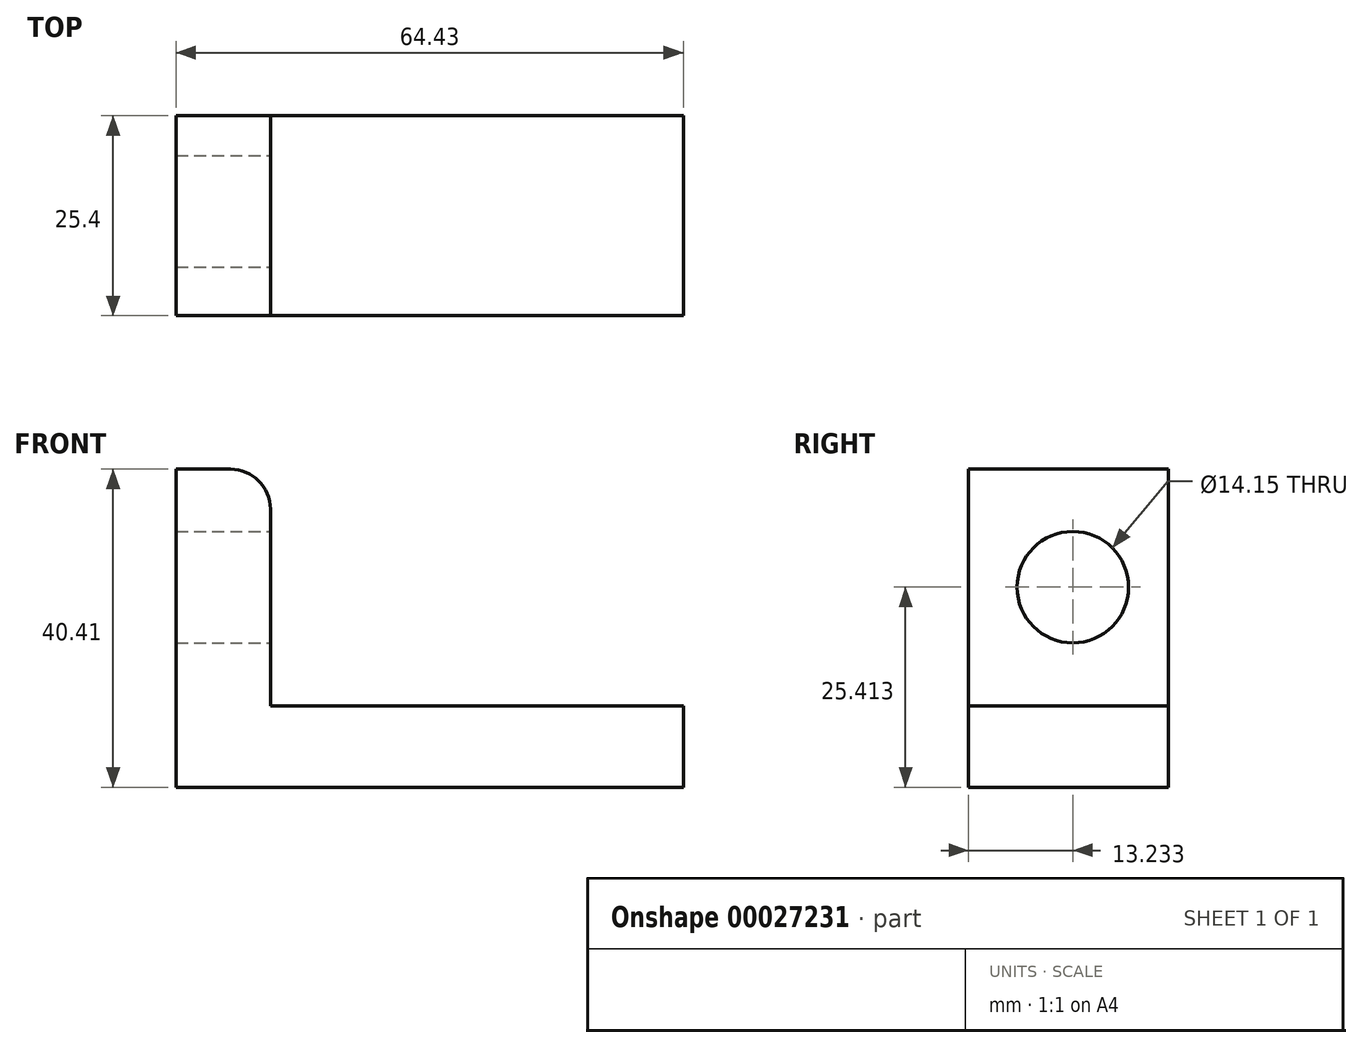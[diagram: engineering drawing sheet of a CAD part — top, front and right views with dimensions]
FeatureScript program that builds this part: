
annotation { "Feature Type Name" : "Feature", "Feature Type Description" : "" }
export const myFeature = defineFeature(function(context is Context, id is Id, definition is map)
    precondition{}
    {
        {
            var Q0;
            Q0=qCreatedBy(makeId("Front.planeOp"),FACE);
            var sketch = newSketch(context, id + "F0", { "sketchPlane" : qUnion([Q0])});
            skLineSegment(sketch, "E0", {"start": v(0, 0) * mm, "end": v(0, -40.4) * mm});
            skLineSegment(sketch, "E1", {"start": v(0, -40.4) * mm, "end": v(64.43, -40.4) * mm});
            skLineSegment(sketch, "E2", {"start": v(64.43, -40.4) * mm, "end": v(64.43, -30.1) * mm});
            skLineSegment(sketch, "E3", {"start": v(64.43, -30.1) * mm, "end": v(11.97, -30.1) * mm});
            skLineSegment(sketch, "E4", {"start": v(11.97, -30.1) * mm, "end": v(11.97, 0) * mm});
            skLineSegment(sketch, "E5", {"start": v(11.97, 0) * mm, "end": v(0, 0) * mm});
            skSolve(sketch);
        }
        {
            var Q0;
            Q0 = qSketchRegion(id + "F0", true);
            extrude(context, id + "F1", {"entities" : qUnion([Q0]), "depth" : 25.4 * mm});
        }
        {
            var Q0;
            Q0=makeQuery(id+"F1.opExtrude","SWEPT_FACE",FACE,{"disambiguationData":[OSD([sQuery(id+"F0.wireOp",EDGE,"E4")])]});
            var sketch = newSketch(context, id + "F2", { "sketchPlane" : qUnion([Q0])});
            skCircle(sketch, "E6", {"center": v(-12.17, -15) * mm, "radius": 7.08 * mm});
            skSolve(sketch);
        }
        {
            var Q0;
            Q0 = qSketchRegion(id + "F2", true);
            extrude(context, id + "F3", {"entities" : qUnion([Q0]), "operationType" : NewBodyOperationType.REMOVE, "oppositeDirection" : true, "depth" : 25.4 * mm});
        }
        {
            var Q0;
            Q0=makeQuery(id+"F1.opExtrude","SWEPT_EDGE",EDGE,{"disambiguationData":[OSD([sQuery(id+"F0.wireOp",EDGE,"E4"),sQuery(id+"F0.wireOp",EDGE,"E5")])]});
            fillet(context, id + "F4", {"entities" : qUnion([Q0]), "radius" : 5.08 * mm, "tangentPropagation" : true, "allowEdgeOverflow" : false});
        }
    });
